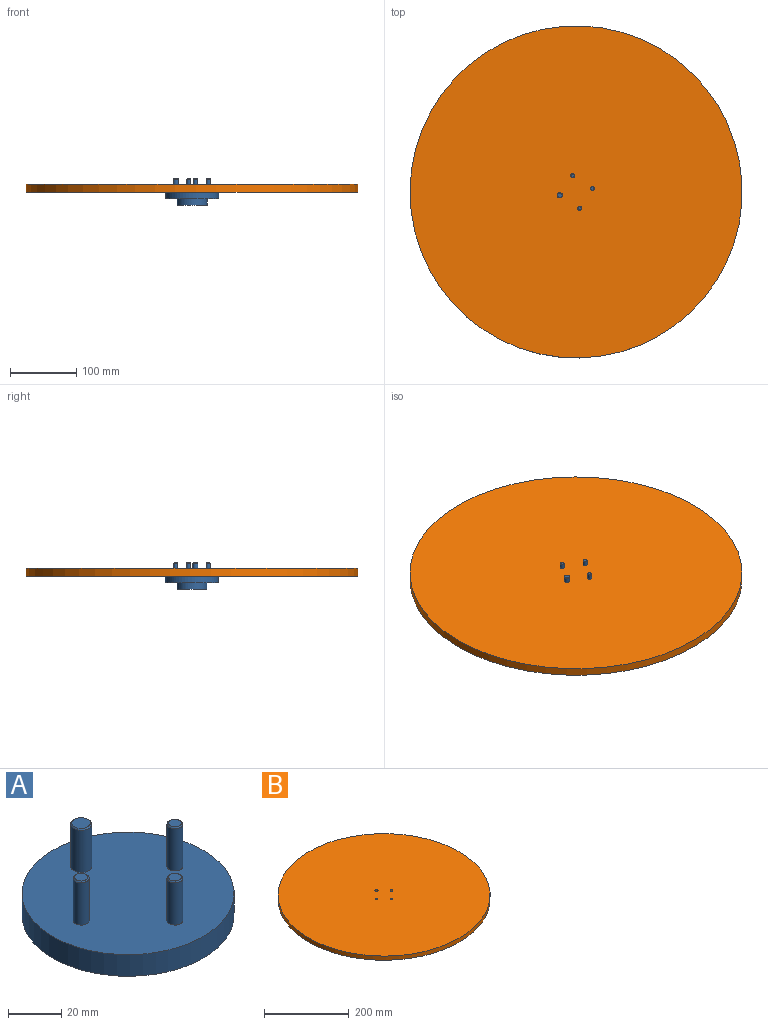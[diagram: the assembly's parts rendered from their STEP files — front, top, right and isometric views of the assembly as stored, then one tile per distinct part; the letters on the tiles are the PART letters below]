
ASSEMBLY  parts=2 mates=1
PART A: 17 faces, bbox 80x80x40 mm
  f0: cylinder r=22.5mm len=45mm, axis (0,0,-1), area 1413.7mm2, adj f1,f4
  f1: plane 45x45mm, normal (0,0,-1), area 1590.4mm2, adj f0
  f2: cylinder r=40mm len=80mm, axis (0,0,-1), area 2513.3mm2, adj f3,f4
  f3: plane 80x80mm, normal (0,0,1), area 4891.5mm2, adj f2,f5,f7,f9,f11
  f4: plane 80x80mm, normal (0,0,-1), area 3436.1mm2, adj f0,f2
  f5: cylinder r=4mm len=19.5mm, axis (0,0,-1), area 490.1mm2, adj f3,f16
  f6: plane 7x7mm, normal (0,0,1), area 38.5mm2, adj f16
  f7: cylinder r=3mm len=19.5mm, axis (0,0,-1), area 367.6mm2, adj f3,f15
  f8: plane 5x5mm, normal (0,0,1), area 19.6mm2, adj f15
  f9: cylinder r=3mm len=19.5mm, axis (0,0,-1), area 367.6mm2, adj f3,f13
  f10: plane 5x5mm, normal (0,0,1), area 19.6mm2, adj f13
  f11: cylinder r=3mm len=19.5mm, axis (0,0,-1), area 367.6mm2, adj f3,f14
  f12: plane 5x5mm, normal (0,0,1), area 19.6mm2, adj f14
  f13: cone r=2.5mm half-angle=45deg, axis (0,0,-1), area 12.2mm2, adj f9,f10
  f14: cone r=2.5mm half-angle=45deg, axis (0,0,-1), area 12.2mm2, adj f11,f12
  f15: cone r=2.5mm half-angle=45deg, axis (0,0,-1), area 12.2mm2, adj f7,f8
  f16: cone r=3.5mm half-angle=45deg, axis (0,0,-1), area 16.7mm2, adj f5,f6
PART B: 7 faces, bbox 500x500x12 mm
  f0: cylinder r=250mm len=500mm, axis (0,0,-1), area 18849.6mm2, adj f1,f2
  f1: plane 500x500mm, normal (0,0,1), area 196214.5mm2, adj f0,f3,f4,f5,f6
  f2: plane 500x500mm, normal (0,0,-1), area 196214.5mm2, adj f0,f3,f4,f5,f6
  f3: cylinder r=3mm len=12mm, axis (0,0,1), area 226.2mm2, adj f1,f2
  f4: cylinder r=3mm len=12mm, axis (0,0,1), area 226.2mm2, adj f1,f2
  f5: cylinder r=3mm len=12mm, axis (0,0,1), area 226.2mm2, adj f1,f2
  f6: cylinder r=4mm len=12mm, axis (0,0,1), area 301.6mm2, adj f1,f2
PLACE A rot(axis=(0,0,1),101.8deg) t=(0,0,0)mm
PLACE B rot(axis=(0,0,1),101.8deg) t=(0,0,20)mm
MATE fastened A.f5 <-> B.f6  axis (0,0,1) through (-24.47,-5.11,20)mm
